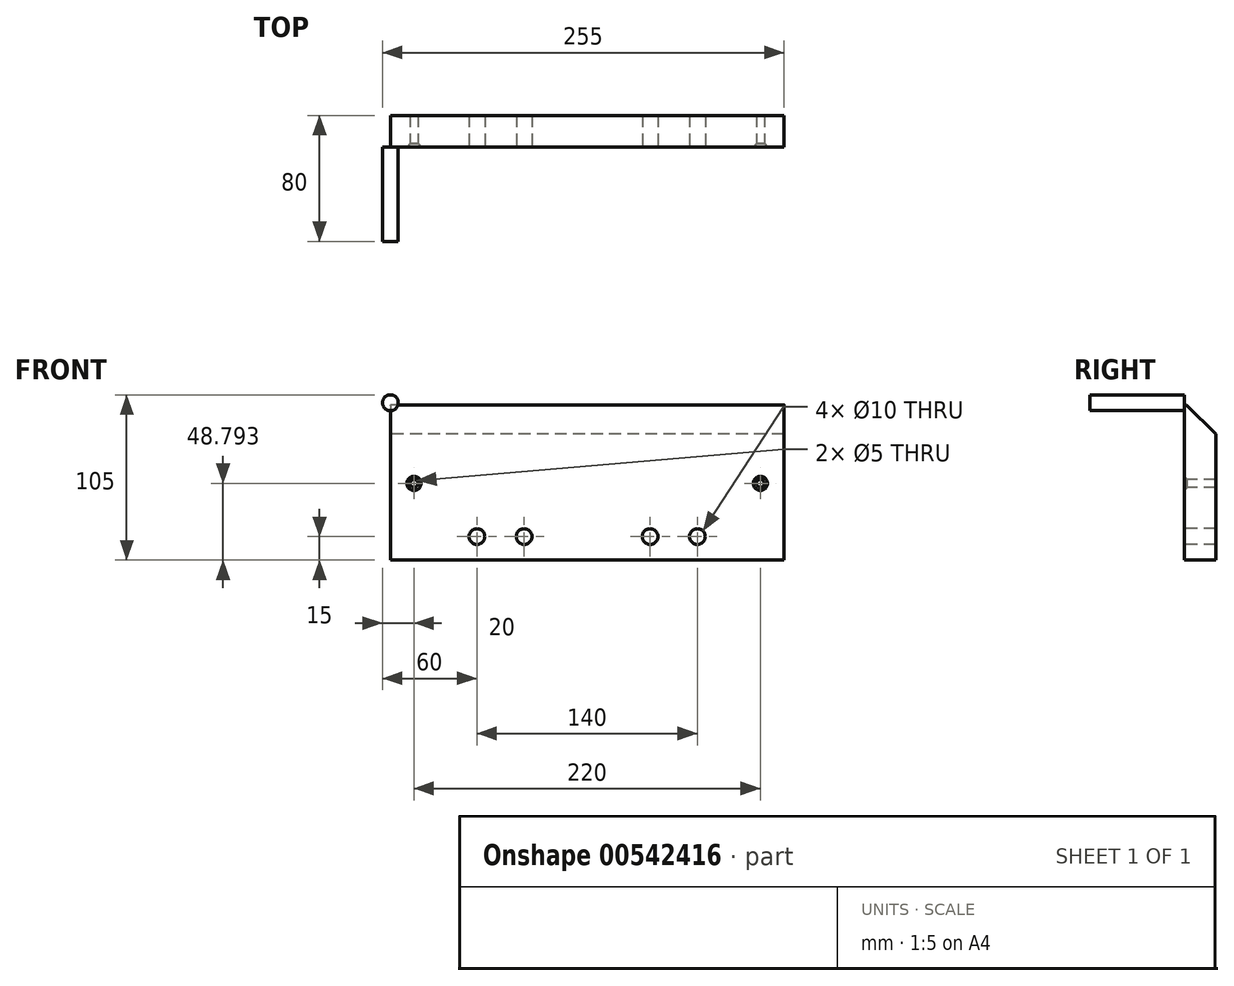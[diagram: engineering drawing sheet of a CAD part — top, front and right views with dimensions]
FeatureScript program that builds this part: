
annotation { "Feature Type Name" : "Feature", "Feature Type Description" : "" }
export const myFeature = defineFeature(function(context is Context, id is Id, definition is map)
    precondition{}
    {
        {
            var Q0;
            Q0=qCreatedBy(makeId("Right.planeOp"),FACE);
            var sketch = newSketch(context, id + "F0", { "sketchPlane" : qUnion([Q0])});
            skLineSegment(sketch, "E0.bottom", {"start": v(1.7, -1.7) * mm, "end": v(20, -20) * mm});
            skLineSegment(sketch, "E0.top", {"start": v(0, -100) * mm, "end": v(20, -100) * mm});
            skLineSegment(sketch, "E0.left", {"start": v(0, -2.41) * mm, "end": v(0, -100) * mm});
            skLineSegment(sketch, "E0.right", {"start": v(20, -20) * mm, "end": v(20, -100) * mm});
            skPoint(sketch, "E1.visualSharp", {"position": v(0, 0) * mm});
            skArc(sketch, "E1.filletArc", {"start": v(1.7, -1.7) * mm, "mid": v(0.62, -1.5) * mm, "end": v(0, -2.41) * mm});
            skSolve(sketch);
        }
        {
            var Q0;
            Q0 = qSketchRegion(id + "F0", true);
            extrude(context, id + "F1", {"entities" : qUnion([Q0]), "depth" : 250 * mm, "offsetDistance" : 25 * mm});
        }
        {
            var Q0;
            Q0=makeQuery(id+"F1.opExtrude","SWEPT_FACE",FACE,{"disambiguationData":[OSD([sQuery(id+"F0.wireOp",EDGE,"E0.left")])]});
            var sketch = newSketch(context, id + "F2", { "sketchPlane" : qUnion([Q0])});
            skLineSegment(sketch, "E2", {"start": v(0, -85) * mm, "end": v(250, -85) * mm, "construction": true});
            skPoint(sketch, "E3", {"position": v(125, -85) * mm});
            skLineSegment(sketch, "E4", {"start": v(125, -151.91) * mm, "end": v(125, -2.41) * mm, "construction": true});
            skPoint(sketch, "E5", {"position": v(55, -85) * mm});
            skPoint(sketch, "E6", {"position": v(85, -85) * mm});
            skPoint(sketch, "E7.MirrorP", {"position": v(195, -85) * mm});
            skPoint(sketch, "E8.MirrorP", {"position": v(165, -85) * mm});
            skSolve(sketch);
        }
        {
            var Q0;
            Q0=makeQuery(id+"F1.opExtrude","SWEPT_FACE",FACE,{"disambiguationData":[OSD([sQuery(id+"F0.wireOp",EDGE,"E0.left")])]});
            var sketch = newSketch(context, id + "F3", { "sketchPlane" : qUnion([Q0])});
            skLineSegment(sketch, "E9", {"start": v(0, -51.2) * mm, "end": v(250, -51.2) * mm, "construction": true});
            skPoint(sketch, "E10", {"position": v(15, -51.2) * mm});
            skPoint(sketch, "E11", {"position": v(235, -51.2) * mm});
            skSolve(sketch);
        }
        {
            var Q0;
            Q0=sQuery(id+"F2.wireOp",VERTEX,"E5");
            var Q1;
            Q1=sQuery(id+"F2.wireOp",VERTEX,"E6");
            var Q2;
            Q2=sQuery(id+"F2.wireOp",VERTEX,"E8.MirrorP");
            var Q3;
            Q3=sQuery(id+"F2.wireOp",VERTEX,"E7.MirrorP");
            var Q4;
            Q4=makeQuery(id+"F1.opExtrude","SWEPT_BODY",BODY,{"disambiguationData":[OSD([sQuery(id+"F0.wireOp",EDGE,"E0.bottom"),sQuery(id+"F0.wireOp",EDGE,"E0.top"),sQuery(id+"F0.wireOp",EDGE,"E0.left"),sQuery(id+"F0.wireOp",EDGE,"E0.right"),sQuery(id+"F0.wireOp",EDGE,"E1.filletArc")])]});
            hole(context, id + "F4", {"style" : HoleStyle.SIMPLE, "endStyle" : HoleEndStyle.THROUGH, "holeDiameter" : 10 * mm, "isTappedThrough" : true, "tappedDepth" : 12 * mm, "tapClearance" : 3, "startFromSketch" : true, "locations" : qUnion([Q0, Q1, Q2, Q3]), "scope" : qUnion([Q4])});
        }
        {
            var Q0;
            Q0=sQuery(id+"F3.wireOp",VERTEX,"E10");
            var Q1;
            Q1=sQuery(id+"F3.wireOp",VERTEX,"E11");
            var Q2;
            Q2=makeQuery(id+"F1.opExtrude","SWEPT_BODY",BODY,{"disambiguationData":[OSD([sQuery(id+"F0.wireOp",EDGE,"E0.bottom"),sQuery(id+"F0.wireOp",EDGE,"E0.top"),sQuery(id+"F0.wireOp",EDGE,"E0.left"),sQuery(id+"F0.wireOp",EDGE,"E0.right"),sQuery(id+"F0.wireOp",EDGE,"E1.filletArc")])]});
            hole(context, id + "F5", {"style" : HoleStyle.C_SINK, "endStyle" : HoleEndStyle.THROUGH, "holeDiameter" : 5 * mm, "cSinkDiameter" : 9 * mm, "cSinkAngle" : 90 * degree, "isTappedThrough" : true, "tappedDepth" : 12 * mm, "tapClearance" : 3, "startFromSketch" : true, "locations" : qUnion([Q0, Q1]), "scope" : qUnion([Q2])});
        }
        {
            var Q0;
            Q0=qCreatedBy(makeId("Front.planeOp"),FACE);
            var sketch = newSketch(context, id + "F6", { "sketchPlane" : qUnion([Q0])});
            skCircle(sketch, "E12", {"center": v(0, 0) * mm, "radius": 5 * mm});
            skSolve(sketch);
        }
        {
            var Q0;
            Q0 = qSketchRegion(id + "F6", true);
            extrude(context, id + "F7", {"entities" : qUnion([Q0]), "depth" : 60 * mm, "offsetDistance" : 25 * mm});
        }
    });
